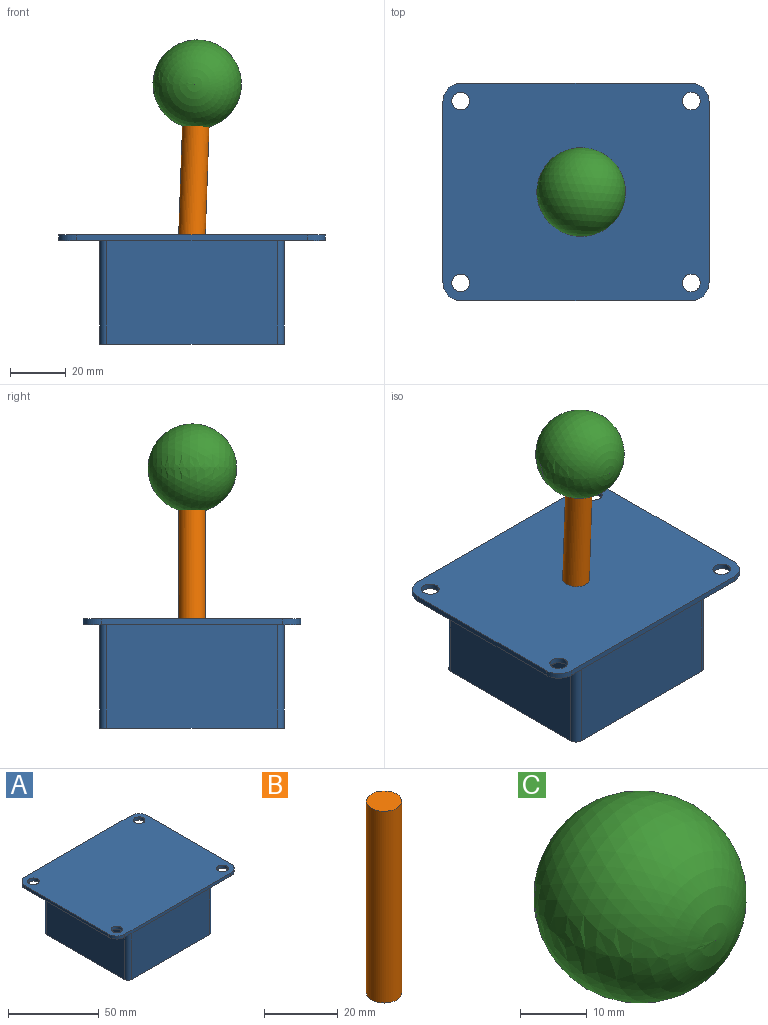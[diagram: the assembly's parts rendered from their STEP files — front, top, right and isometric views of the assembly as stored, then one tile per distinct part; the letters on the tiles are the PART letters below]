
ASSEMBLY  parts=3 mates=2
PART A: 23 faces, bbox 95.3x77.8x39.1 mm
  f0: plane 65.09x2.03mm, normal (-1,0,0), area 132.3mm2, adj f1,f11,f12,f13
  f1: cylinder r=6.35mm len=6.35mm, axis (0,0,1), area 20.3mm2, adj f0,f2,f12,f13
  f2: plane 82.55x2.03mm, normal (0,-1,0), area 167.7mm2, adj f1,f3,f12,f13
  f3: cylinder r=6.35mm len=6.35mm, axis (0,0,1), area 20.3mm2, adj f2,f4,f12,f13
  f4: plane 65.09x2.03mm, normal (1,0,0), area 132.3mm2, adj f3,f5,f12,f13
  f5: cylinder r=6.35mm len=6.35mm, axis (0,0,1), area 20.3mm2, adj f4,f6,f12,f13
  f6: plane 82.55x2.03mm, normal (0,1,0), area 167.7mm2, adj f5,f11,f12,f13
  f7: cylinder r=3.17mm len=6.35mm, axis (0,0,1), area 40.5mm2, adj f12,f13
  f8: cylinder r=3.17mm len=6.35mm, axis (0,0,1), area 40.5mm2, adj f12,f13
  f9: cylinder r=3.17mm len=6.35mm, axis (0,0,1), area 40.5mm2, adj f12,f13
  f10: cylinder r=3.17mm len=6.35mm, axis (0,0,1), area 40.5mm2, adj f12,f13
  f11: cylinder r=6.35mm len=6.35mm, axis (0,0,1), area 20.3mm2, adj f0,f6,f12,f13
  f12: plane 95.25x77.79mm, normal (0,0,-1), area 2892.2mm2, adj f0,f1,f2,f3,f4,f5,f6,f7
  f13: plane 95.25x77.79mm, normal (0,0,1), area 7248mm2, adj f0,f1,f2,f3,f4,f5,f6,f7
  f14: plane 60.96x37.08mm, normal (-1,0,0), area 2260.6mm2, adj f12,f15,f21,f22
  f15: cylinder r=2.54mm len=37.08mm, axis (0,0,1), area 148mm2, adj f12,f14,f16,f22
  f16: plane 60.96x37.08mm, normal (0,1,0), area 2260.6mm2, adj f12,f15,f17,f22
  f17: cylinder r=2.54mm len=37.08mm, axis (0,0,1), area 148mm2, adj f12,f16,f18,f22
  f18: plane 60.96x37.08mm, normal (1,0,0), area 2260.6mm2, adj f12,f17,f19,f22
  f19: cylinder r=2.54mm len=37.08mm, axis (0,0,1), area 148mm2, adj f12,f18,f20,f22
  f20: plane 60.96x37.08mm, normal (0,-1,0), area 2260.6mm2, adj f12,f19,f21,f22
  f21: cylinder r=2.54mm len=37.08mm, axis (0,0,1), area 148mm2, adj f12,f14,f20,f22
  f22: plane 66.04x66.04mm, normal (0,0,-1), area 4355.7mm2, adj f14,f15,f16,f17,f18,f19,f20,f21
PART B: 3 faces, bbox 9.5x9.5x63.5 mm
  f0: cylinder r=4.76mm len=63.5mm, axis (0,0,-1), area 1900.2mm2, adj f1,f2
  f1: plane 9.53x9.53mm, normal (0,0,1), area 71.3mm2, adj f0
  f2: plane 9.53x9.53mm, normal (0,0,-1), area 71.3mm2, adj f0
PART C: 1 faces, bbox 31.8x31.8x31.8 mm
  f0: sphere r=15.88mm, area 3166.9mm2
PLACE A t=(-6.15,-2.16,11.66)mm fixed
PLACE B rot(axis=(0.02,0.48,-0.87),4.1deg) t=(-56.33,-69.48,13.25)mm
PLACE C rot(axis=(0.02,0.48,-0.87),4.1deg) t=(-8.69,-72.48,65.6)mm
MATE fastened B.f0 <-> C.f0  axis (0.03,0,1) through (-3.94,-2.29,75.12)mm
MATE ball B.f0 <-> A.f13  axis (-0.03,0,-1) through (-6.15,-2.16,11.66)mm
